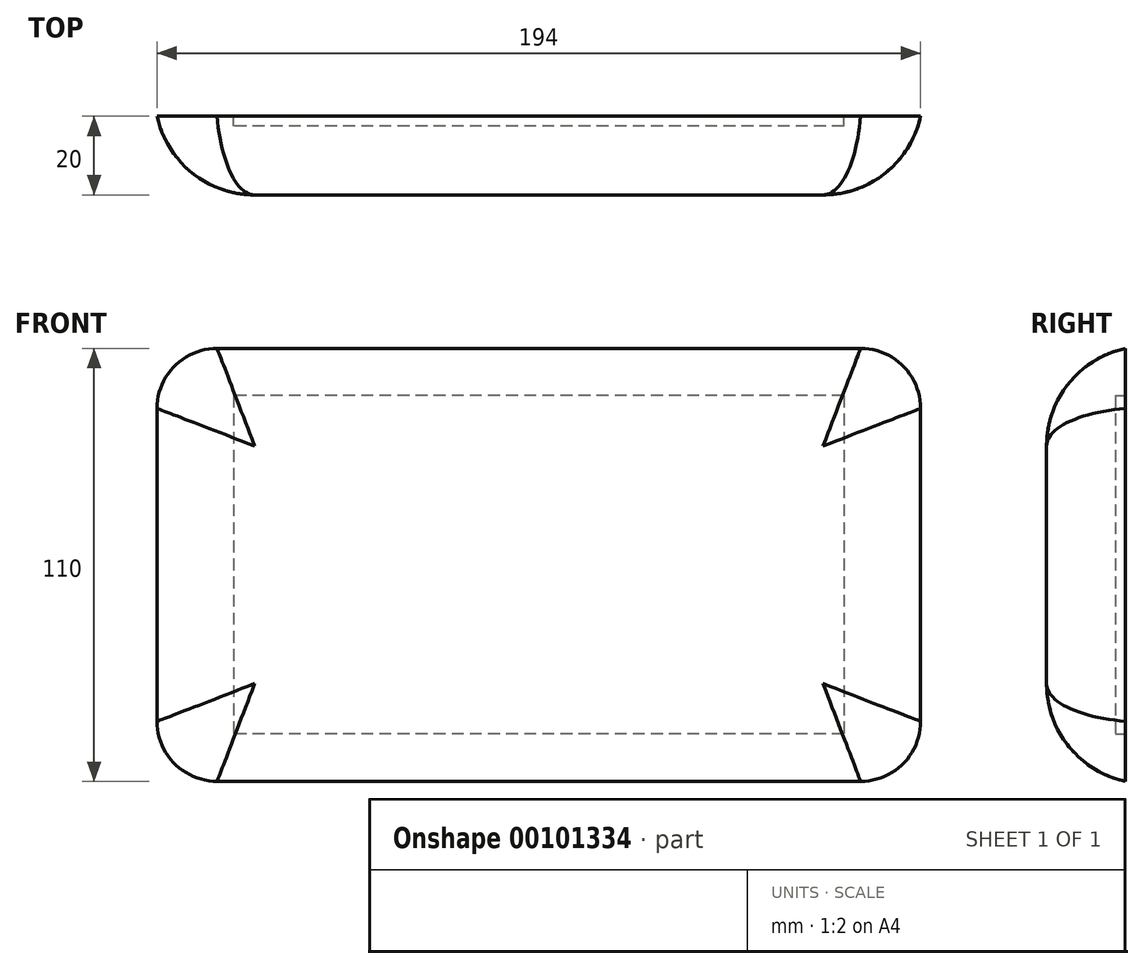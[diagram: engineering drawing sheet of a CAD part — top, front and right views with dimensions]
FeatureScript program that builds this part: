
annotation { "Feature Type Name" : "Feature", "Feature Type Description" : "" }
export const myFeature = defineFeature(function(context is Context, id is Id, definition is map)
    precondition{}
    {
        {
            var Q0;
            Q0=qCreatedBy(makeId("Front.planeOp"),FACE);
            var sketch = newSketch(context, id + "F0", { "sketchPlane" : qUnion([Q0])});
            skLineSegment(sketch, "E0.bottom", {"start": v(-97, 55) * mm, "end": v(97, 55) * mm});
            skLineSegment(sketch, "E0.top", {"start": v(-97, -55) * mm, "end": v(97, -55) * mm});
            skLineSegment(sketch, "E0.left", {"start": v(-97, 55) * mm, "end": v(-97, -55) * mm});
            skLineSegment(sketch, "E0.right", {"start": v(97, 55) * mm, "end": v(97, -55) * mm});
            skSolve(sketch);
        }
        {
            var Q0;
            Q0 = qSketchRegion(id + "F0", true);
            extrude(context, id + "F1", {"entities" : qUnion([Q0]), "depth" : 20 * mm});
        }
        {
            var Q0;
            Q0=makeQuery(id+"F1.opExtrude","CAP_FACE",FACE,{"disambiguationData":[OSD([sQuery(id+"F0.wireOp",EDGE,"E0.bottom"),sQuery(id+"F0.wireOp",EDGE,"E0.top"),sQuery(id+"F0.wireOp",EDGE,"E0.left"),sQuery(id+"F0.wireOp",EDGE,"E0.right")])],"isStart":true});
            var sketch = newSketch(context, id + "F2", { "sketchPlane" : qUnion([Q0])});
            skLineSegment(sketch, "E1.bottom", {"start": v(-77.5, 43) * mm, "end": v(77.5, 43) * mm});
            skLineSegment(sketch, "E1.top", {"start": v(-77.5, -43) * mm, "end": v(77.5, -43) * mm});
            skLineSegment(sketch, "E1.left", {"start": v(-77.5, 43) * mm, "end": v(-77.5, -43) * mm});
            skLineSegment(sketch, "E1.right", {"start": v(77.5, 43) * mm, "end": v(77.5, -43) * mm});
            skSolve(sketch);
        }
        {
            var Q0;
            Q0 = qSketchRegion(id + "F2", true);
            extrude(context, id + "F3", {"entities" : qUnion([Q0]), "operationType" : NewBodyOperationType.REMOVE, "oppositeDirection" : true, "depth" : 2.54 * mm});
        }
        {
            var Q0;
            Q0=makeQuery(id+"F1.opExtrude","SWEPT_EDGE",EDGE,{"disambiguationData":[OSD([sQuery(id+"F0.wireOp",EDGE,"E0.bottom"),sQuery(id+"F0.wireOp",EDGE,"E0.left")])]});
            var Q1;
            Q1=makeQuery(id+"F1.opExtrude","SWEPT_EDGE",EDGE,{"disambiguationData":[OSD([sQuery(id+"F0.wireOp",EDGE,"E0.bottom"),sQuery(id+"F0.wireOp",EDGE,"E0.right")])]});
            var Q2;
            Q2=makeQuery(id+"F1.opExtrude","SWEPT_EDGE",EDGE,{"disambiguationData":[OSD([sQuery(id+"F0.wireOp",EDGE,"E0.top"),sQuery(id+"F0.wireOp",EDGE,"E0.right")])]});
            var Q3;
            Q3=makeQuery(id+"F1.opExtrude","SWEPT_EDGE",EDGE,{"disambiguationData":[OSD([sQuery(id+"F0.wireOp",EDGE,"E0.top"),sQuery(id+"F0.wireOp",EDGE,"E0.left")])]});
            fillet(context, id + "F4", {"entities" : qUnion([Q0, Q1, Q2, Q3]), "radius" : 15.24 * mm, "tangentPropagation" : true, "allowEdgeOverflow" : false});
        }
        {
            var Q0;
            Q0=makeQuery(id+"F1.opExtrude","CAP_EDGE",EDGE,{"disambiguationData":[OSD([sQuery(id+"F0.wireOp",EDGE,"E0.right")])],"isStart":false});
            var Q1;
            {var subQ0=sQuery(id+"F0.wireOp",EDGE,"E0.right");var subQ1=sQuery(id+"F0.wireOp",EDGE,"E0.bottom");Q1=makeQuery(id+"F4.opFillet","BLEND_EDGE",EDGE,{"blendedFrom":[makeQuery(id+"F1.opExtrude","SWEPT_EDGE",EDGE,{"disambiguationData":[OSD([subQ1,subQ0])]}),makeQuery(id+"F1.opExtrude","CAP_FACE",FACE,{"disambiguationData":[OSD([subQ1,sQuery(id+"F0.wireOp",EDGE,"E0.top"),sQuery(id+"F0.wireOp",EDGE,"E0.left"),subQ0])],"isStart":false})],"blendedInto":[makeQuery(id+"F1.opExtrude","CAP_FACE",FACE,{"disambiguationData":[OSD([subQ1,sQuery(id+"F0.wireOp",EDGE,"E0.top"),sQuery(id+"F0.wireOp",EDGE,"E0.left"),subQ0])],"isStart":false})]});}
            var Q2;
            Q2=makeQuery(id+"F1.opExtrude","CAP_EDGE",EDGE,{"disambiguationData":[OSD([sQuery(id+"F0.wireOp",EDGE,"E0.bottom")])],"isStart":false});
            var Q3;
            {var subQ0=sQuery(id+"F0.wireOp",EDGE,"E0.right");var subQ1=sQuery(id+"F0.wireOp",EDGE,"E0.top");Q3=makeQuery(id+"F4.opFillet","BLEND_EDGE",EDGE,{"blendedFrom":[makeQuery(id+"F1.opExtrude","SWEPT_EDGE",EDGE,{"disambiguationData":[OSD([subQ1,subQ0])]}),makeQuery(id+"F1.opExtrude","CAP_FACE",FACE,{"disambiguationData":[OSD([sQuery(id+"F0.wireOp",EDGE,"E0.bottom"),subQ1,sQuery(id+"F0.wireOp",EDGE,"E0.left"),subQ0])],"isStart":false})],"blendedInto":[makeQuery(id+"F1.opExtrude","CAP_FACE",FACE,{"disambiguationData":[OSD([sQuery(id+"F0.wireOp",EDGE,"E0.bottom"),subQ1,sQuery(id+"F0.wireOp",EDGE,"E0.left"),subQ0])],"isStart":false})]});}
            var Q4;
            Q4=makeQuery(id+"F1.opExtrude","CAP_EDGE",EDGE,{"disambiguationData":[OSD([sQuery(id+"F0.wireOp",EDGE,"E0.top")])],"isStart":false});
            var Q5;
            {var subQ0=sQuery(id+"F0.wireOp",EDGE,"E0.left");var subQ1=sQuery(id+"F0.wireOp",EDGE,"E0.top");Q5=makeQuery(id+"F4.opFillet","BLEND_EDGE",EDGE,{"blendedFrom":[makeQuery(id+"F1.opExtrude","SWEPT_EDGE",EDGE,{"disambiguationData":[OSD([subQ1,subQ0])]}),makeQuery(id+"F1.opExtrude","CAP_FACE",FACE,{"disambiguationData":[OSD([sQuery(id+"F0.wireOp",EDGE,"E0.bottom"),subQ1,subQ0,sQuery(id+"F0.wireOp",EDGE,"E0.right")])],"isStart":false})],"blendedInto":[makeQuery(id+"F1.opExtrude","CAP_FACE",FACE,{"disambiguationData":[OSD([sQuery(id+"F0.wireOp",EDGE,"E0.bottom"),subQ1,subQ0,sQuery(id+"F0.wireOp",EDGE,"E0.right")])],"isStart":false})]});}
            var Q6;
            Q6=makeQuery(id+"F1.opExtrude","CAP_EDGE",EDGE,{"disambiguationData":[OSD([sQuery(id+"F0.wireOp",EDGE,"E0.left")])],"isStart":false});
            var Q7;
            {var subQ0=sQuery(id+"F0.wireOp",EDGE,"E0.left");var subQ1=sQuery(id+"F0.wireOp",EDGE,"E0.bottom");Q7=makeQuery(id+"F4.opFillet","BLEND_EDGE",EDGE,{"blendedFrom":[makeQuery(id+"F1.opExtrude","SWEPT_EDGE",EDGE,{"disambiguationData":[OSD([subQ1,subQ0])]}),makeQuery(id+"F1.opExtrude","CAP_FACE",FACE,{"disambiguationData":[OSD([subQ1,sQuery(id+"F0.wireOp",EDGE,"E0.top"),subQ0,sQuery(id+"F0.wireOp",EDGE,"E0.right")])],"isStart":false})],"blendedInto":[makeQuery(id+"F1.opExtrude","CAP_FACE",FACE,{"disambiguationData":[OSD([subQ1,sQuery(id+"F0.wireOp",EDGE,"E0.top"),subQ0,sQuery(id+"F0.wireOp",EDGE,"E0.right")])],"isStart":false})]});}
            fillet(context, id + "F5", {"entities" : qUnion([Q0, Q1, Q2, Q3, Q4, Q5, Q6, Q7]), "radius" : 25.4 * mm, "tangentPropagation" : true, "allowEdgeOverflow" : false});
        }
    });
